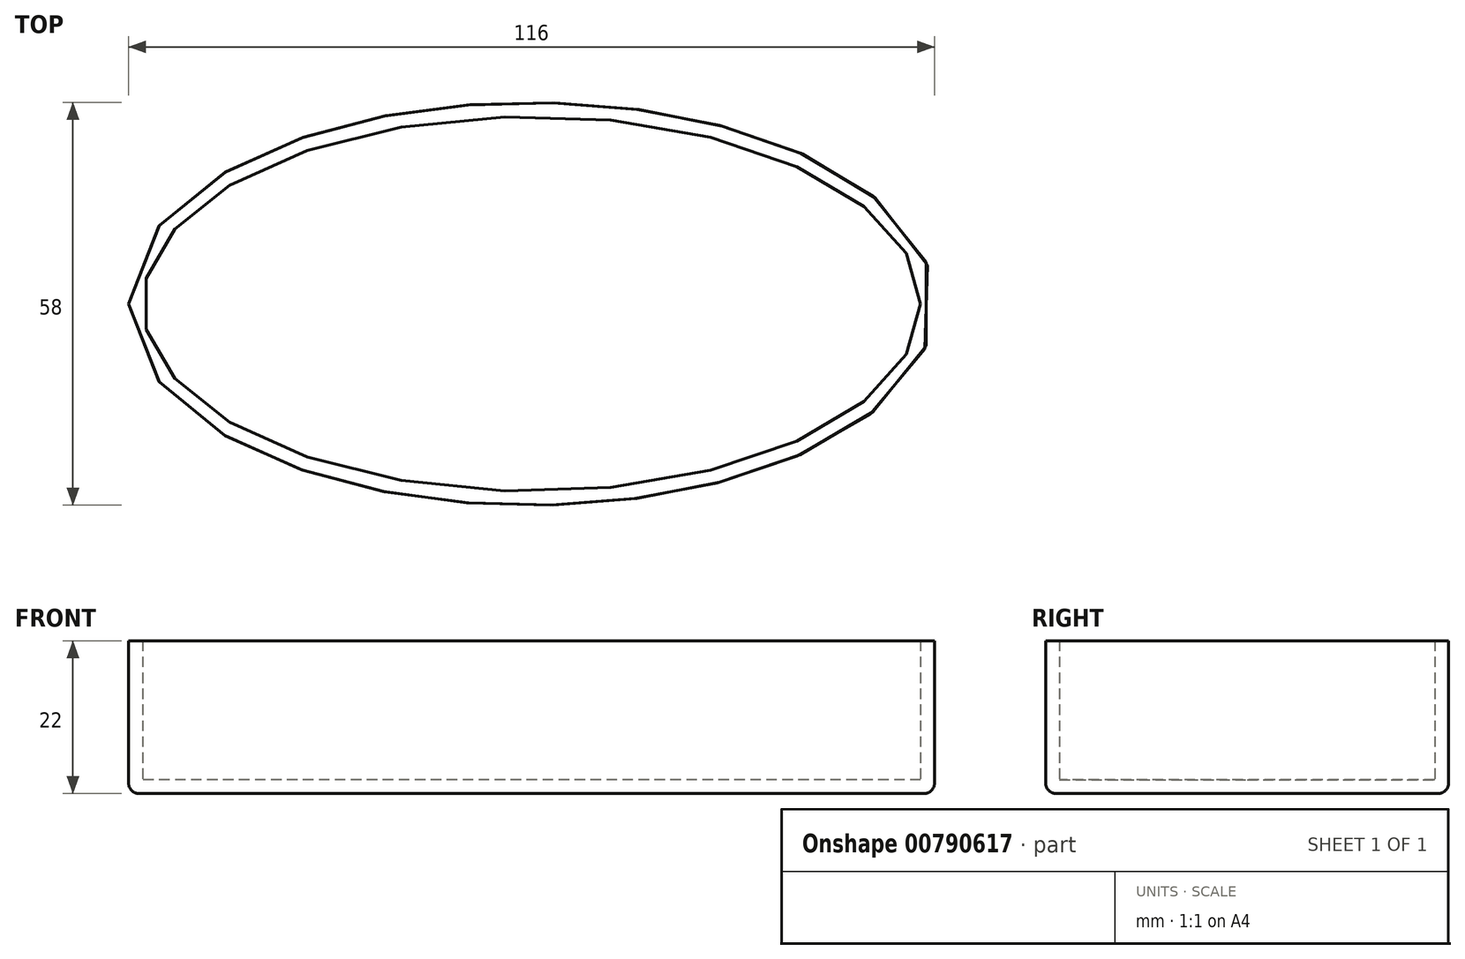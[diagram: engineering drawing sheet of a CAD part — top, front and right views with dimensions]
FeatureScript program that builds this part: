
annotation { "Feature Type Name" : "Feature", "Feature Type Description" : "" }
export const myFeature = defineFeature(function(context is Context, id is Id, definition is map)
    precondition{}
    {
        {
            var Q0;
            Q0=qCreatedBy(makeId("Top.planeOp"),FACE);
            var sketch = newSketch(context, id + "F0", { "sketchPlane" : qUnion([Q0])});
            skEllipse(sketch, "E0", {"center": v(0, 0) * mm, "majorRadius": 56 * mm, "minorRadius": 27 * mm, "majorAxis": v(1, 0)});
            skSolve(sketch);
        }
        {
            var Q0;
            Q0=makeQuery(id+"F0.imprint","IMPRINT",FACE,{"disambiguationData":[TD([[makeQuery(id+"F0.imprint","IMPRINT",EDGE,{"derivedFrom":sQuery(id+"F0.wireOp",EDGE,"E0")}),1.0]])]});
            extrude(context, id + "F1", {"entities" : qUnion([Q0]), "depth" : 20 * mm, "offsetDistance" : 25 * mm});
        }
        {
            var Q0;
            Q0=makeQuery(id+"F1.opExtrude","CAP_FACE",FACE,{"disambiguationData":[OSD([sQuery(id+"F0.wireOp",EDGE,"E0")])],"isStart":false});
            shell(context, id + "F2", {"entities" : qUnion([Q0]), "thickness" : 2 * mm, "oppositeDirection" : true});
        }
        {
            var Q0;
            Q0=makeQuery(id+"F1.opExtrude","CAP_EDGE",EDGE,{"disambiguationData":[OSD([sQuery(id+"F0.wireOp",EDGE,"E0")])],"isStart":true});
            fillet(context, id + "F3", {"entities" : qUnion([Q0]), "radius" : 1.5 * mm, "tangentPropagation" : true, "allowEdgeOverflow" : false});
        }
    });
